# Revit family: M2WU
name_source: partatom
category: Lighting Fixtures
revit_build: Autodesk Revit Architecture 2012 (Build: 20110309_2315(x64)
units: mm (PartAtom-declared; Revit-internal decimal feet)

## types (22) — shared parameters
Apparent Load = 0 VA
Color Filter = 16777215
Default Elevation = 60"
Description = Horizontal reflector uplight
Dimming Lamp Color Temperature Shift = <None>
Finish = Die Cast Aluminium
Finish 2 = Silicon Gasket
Glass = Glass-Finish
Lamp = One
Manufacturer = Architectural Area Lighting
Manufacturer Fax = 626-369-2695
Model = M2WU
Product Documentation Link = http://www.aal.net
Product Page URL = http://www.aal.net
Tilt Angle = 90.00°
URL = www.aal.net
Voltage = 120 V
Wattage Comments = 57 and 70 watts High Output Fluorescent

## per-type parameters (varying)
| type | Photometric Web File |
| M2WU-T2-32LED-3K-700 | M2-T2-32LED-3K-700.ies |
| M2WU-T3-32LED-3K-700 | M2-T3-32LED-3K-700.ies |
| M2WU-T4-32LED-3K-700 | M2-T4-32LED-3K-700.ies |
| M2WU-T4-32LED-3K-HSS-700 | M2-T4-32LED-3K-HSS-700.ies |
| M2WU-T5-32LED-3K-700 | M2-T5-32LED-3K-700.ies |
| M2WU-TL-32LED-3K-700 | M2-TL-32LED-3K-700.ies |
| M2WU-TR-32LED-3K-700 | M2-TR-32LED-3K-700.ies |
| M2WU-T2-32LED-4K-700 | M2-T2-32LED-4K-700.ies |
| M2WU-T3-32LED-4K-700 | M2-T3-32LED-4K-700.ies |
| M2WU-T4-32LED-4K-700 | M2-T4-32LED-4K-700.ies |
| M2WU-T4-32LED-4K-HSS-700 | M2-T4-32LED-4K-HSS-700.ies |
| M2WU-T5-32LED-4K-700 | M2-T5-32LED-4K-700.ies |
| M2WU-TL-32LED-4K-700 | M2-TL-32LED-4K-700.ies |
| M2WU-TR-32LED-4K-700 | M2-TR-32LED-4K-700.ies |
| M2WU-T2-32LED-5K-700 | M2-T2-32LED-5K-700.ies |
| M2WU-T2-32LED-5K-HSS-700 | M2-T2-32LED-5K-HSS-700.ies |
| M2WU-T3-32LED-5K-700 | M2-T3-32LED-5K-700.ies |
| M2WU-T4-32LED-5K-700 | M2-T4-32LED-5K-700.ies |
| M2WU-T4-32LED-5K-HSS-700 | M2-T4-32LED-5K-HSS-700.ies |
| M2WU-T5-32LED-5K-700 | M2-T5-32LED-5K-700.ies |
| M2WU-TL-32LED-5K-700 | M2-TL-32LED-5K-700.ies |
| M2WU-TR-32LED-5K-700 | M2-TR-32LED-5K-700.ies |

## geometry (parser evidence)
native form markers: Sweep x5
no freeform markers — native parametric forms only
